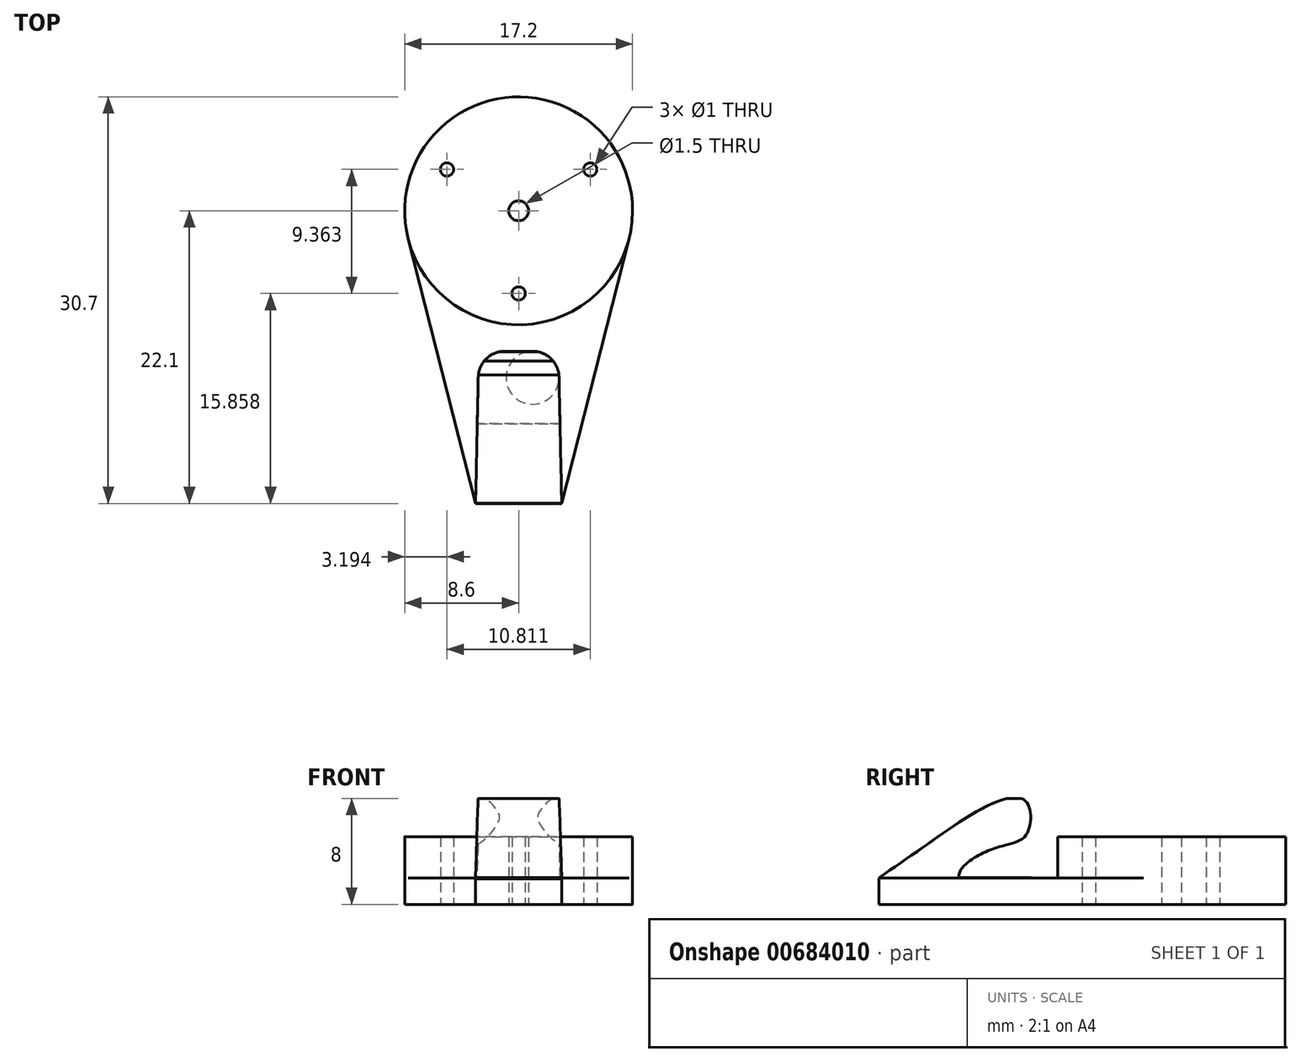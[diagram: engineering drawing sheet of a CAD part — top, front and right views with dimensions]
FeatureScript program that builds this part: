
annotation { "Feature Type Name" : "Feature", "Feature Type Description" : "" }
export const myFeature = defineFeature(function(context is Context, id is Id, definition is map)
    precondition{}
    {
        {
            var Q0;
            Q0=qCreatedBy(makeId("Top.planeOp"),FACE);
            var sketch = newSketch(context, id + "F0", { "sketchPlane" : qUnion([Q0])});
            skCircle(sketch, "E0", {"center": v(0, 0) * mm, "radius": 8.6 * mm});
            skLineSegment(sketch, "E1", {"start": v(-3.25, -22.1) * mm, "end": v(3.25, -22.1) * mm});
            skLineSegment(sketch, "E2", {"start": v(0, 0) * mm, "end": v(0, -34.63) * mm, "construction": true});
            skLineSegment(sketch, "E3", {"start": v(-3.25, -22.1) * mm, "end": v(-8.33, -2.12) * mm});
            skLineSegment(sketch, "E4", {"start": v(3.25, -22.1) * mm, "end": v(8.33, -2.12) * mm});
            skCircle(sketch, "E5", {"center": v(0, 0) * mm, "radius": 0.75 * mm});
            skCircle(sketch, "E6", {"center": v(0, -6.24) * mm, "radius": 0.5 * mm});
            skCircle(sketch, "E7.1.1", {"center": v(5.4, 3.12) * mm, "radius": 0.5 * mm});
            skCircle(sketch, "E7.2.1", {"center": v(-5.4, 3.12) * mm, "radius": 0.5 * mm});
            skSolve(sketch);
        }
        {
            var Q0;
            Q0=makeQuery(id+"F0.imprint","IMPRINT",FACE,{"disambiguationData":[TD([[makeQuery(id+"F0.imprint","IMPRINT",EDGE,{"derivedFrom":sQuery(id+"F0.wireOp",EDGE,"E6")}),-1.0]])]});
            extrude(context, id + "F1", {"entities" : qUnion([Q0]), "depth" : 5.1 * mm, "offsetDistance" : 25 * mm});
        }
        {
            var Q0;
            Q0=makeQuery(id+"F0.imprint","IMPRINT",FACE,{"disambiguationData":[TD([[makeQuery(id+"F0.imprint","IMPRINT",EDGE,{"derivedFrom":sQuery(id+"F0.wireOp",EDGE,"E1")}),1.0]])]});
            extrude(context, id + "F2", {"entities" : qUnion([Q0]), "operationType" : NewBodyOperationType.ADD, "depth" : 2 * mm, "offsetDistance" : 25 * mm});
        }
        {
            var Q0;
            Q0=makeQuery(id+"F2.opExtrude","CAP_FACE",FACE,{"disambiguationData":[OSD([sQuery(id+"F0.wireOp",EDGE,"E0"),sQuery(id+"F0.wireOp",EDGE,"E1"),sQuery(id+"F0.wireOp",EDGE,"E3"),sQuery(id+"F0.wireOp",EDGE,"E4")])],"isStart":false});
            var sketch = newSketch(context, id + "F3", { "sketchPlane" : qUnion([Q0])});
            skLineSegment(sketch, "E8", {"start": v(-3.25, -22.1) * mm, "end": v(-3.05, -12.56) * mm});
            skLineSegment(sketch, "E9", {"start": v(-1.05, -10.6) * mm, "end": v(1.05, -10.6) * mm});
            skLineSegment(sketch, "E10", {"start": v(3.05, -12.56) * mm, "end": v(3.25, -22.1) * mm});
            skPoint(sketch, "E11.visualSharp", {"position": v(-3, -10.6) * mm});
            skArc(sketch, "E11.filletArc", {"start": v(-1.05, -10.6) * mm, "mid": v(-2.45, -11.17) * mm, "end": v(-3.05, -12.56) * mm});
            skPoint(sketch, "E12.visualSharp", {"position": v(3, -10.6) * mm});
            skArc(sketch, "E12.filletArc", {"start": v(3.05, -12.56) * mm, "mid": v(2.45, -11.17) * mm, "end": v(1.05, -10.6) * mm});
            skLineSegment(sketch, "E13", {"start": v(-3.96, -8.6) * mm, "end": v(4.71, -8.6) * mm, "construction": true});
            skPoint(sketch, "E13.endSnap0", {"position": v(0, -8.6) * mm});
            skSolve(sketch);
        }
        {
            var Q0;
            Q0=makeQuery(id+"F3.imprint","IMPRINT",FACE,{"disambiguationData":[TD([[makeQuery(id+"F3.imprint","IMPRINT",EDGE,{"derivedFrom":sQuery(id+"F3.wireOp",EDGE,"E8")}),-1.0]])]});
            extrude(context, id + "F4", {"entities" : qUnion([Q0]), "operationType" : NewBodyOperationType.ADD, "depth" : 6 * mm, "offsetDistance" : 25 * mm});
        }
        {
            var Q0;
            Q0=qCreatedBy(makeId("Right.planeOp"),FACE);
            var sketch = newSketch(context, id + "F5", { "sketchPlane" : qUnion([Q0])});
            skFitSpline(sketch, "E14", {"points": [v(-22.06, 2.03) * mm, v(-13.54, 7.6) * mm, v(-10.99, 7.76) * mm, v(-10.97, 5.26) * mm, v(-13.36, 4.23) * mm, v(-16.06, 2.03) * mm], "startDerivative": vector(39.39, 26.62) * mm, "endDerivative": vector(1.83, -13.4) * mm});
            skLineSegment(sketch, "E15", {"start": v(-22.06, 2.03) * mm, "end": v(-23.04, 0) * mm});
            skLineSegment(sketch, "E16", {"start": v(-23.04, 0) * mm, "end": v(-19.68, -1.62) * mm});
            skLineSegment(sketch, "E17", {"start": v(-19.68, -1.62) * mm, "end": v(-19.68, -1.62) * mm});
            skLineSegment(sketch, "E18", {"start": v(-19.68, -1.62) * mm, "end": v(11.3, -3.42) * mm});
            skLineSegment(sketch, "E19", {"start": v(11.3, -3.42) * mm, "end": v(11.63, 2.24) * mm});
            skLineSegment(sketch, "E20", {"start": v(11.63, 2.24) * mm, "end": v(9.35, 8.46) * mm});
            skLineSegment(sketch, "E21", {"start": v(9.35, 8.46) * mm, "end": v(-3.05, 7.96) * mm});
            skLineSegment(sketch, "E22", {"start": v(-3.05, 7.96) * mm, "end": v(-9.45, 6.16) * mm});
            skLineSegment(sketch, "E23", {"start": v(-9.45, 6.16) * mm, "end": v(-9.54, 4.24) * mm});
            skLineSegment(sketch, "E24", {"start": v(-9.54, 4.24) * mm, "end": v(-10.33, 2.03) * mm});
            skLineSegment(sketch, "E25", {"start": v(-10.33, 2.03) * mm, "end": v(-16.06, 2.03) * mm});
            skSolve(sketch);
        }
        {
            var Q0;
            Q0=makeQuery(id+"F5.imprint","IMPRINT",FACE,{"disambiguationData":[TD([[makeQuery(id+"F5.imprint","IMPRINT",EDGE,{"derivedFrom":sQuery(id+"F5.wireOp",EDGE,"E14")}),-1.0]])]});
            extrude(context, id + "F6", {"entities" : qUnion([Q0]), "operationType" : NewBodyOperationType.INTERSECT, "endBound" : BoundingType.SYMMETRIC, "depth" : 25 * mm, "offsetDistance" : 25 * mm});
        }
    });
